# Revit family: CCIRC Emergency Circular Lighting_UK_Non-Hosted_R20_V1.0
name_source: partatom
category: Lighting Fixtures
units: mm (PartAtom-declared; Revit-internal decimal feet)

## family parameters
Always vertical = Yes
Cut with Voids When Loaded = No
Light Source = Yes
OmniClass Number = 23.80.70.00
OmniClass Title = Lighting
Part Type = Normal
Room Calculation Point = No
Round Connector Dimension = Use Diameter
Shared = No
Work Plane-Based = No

## types (2) — shared parameters
Applicable Standards = BS EN 60598.2.22, BS 5266
Battery Type = Lithium Iron Phosphate (LiFePO4)
Charging Method = Intelligent Current Limited Constant Voltage
Color Filter = 16777215
Construction = Polycarbonate
Diffuser = Polycarbonate Diffuser
Dimensions (L x W x H) = 327mm (Diameter) x 100mm (Height)
Dimming Lamp Color Temperature Shift = <None>
Emergency Lumen Output = 374lm
Emit Shape Visible in Rendering = No
IP Rating = IP54
LED Driver = LED Driver -11W Stallion, 360mA
Lamp = LED module, 4,000K natural white, 50,000h life, Ra>80
Manufacturer = Clevertronics
Mounting = Surface Mount
Operating Mode = Sustained
Operating Temperature = 0˚C to 30˚C
Operating Voltage = 220-240V AC; 50Hz
Photometric Web File = 6002_CCIRC-HV(S4)_EM220mA_23082021-02_IES2002.IES
Power Factor = 0.93
Replacement Battery = 1550230
Replacement Driver = 1330091
Replacement lamp = 8011800
Tilt Angle = 90.00°
Weight = 1.8 kg
zero-valued in all types: Default Elevation

## per-type parameters (varying)
| type | Description | MIC Number | Power Consumption (Lamp ON Max Charge) | Power Consumption (Lamp Off Standby) | Replacement Emergency Driver | Replacement Item | Testing System | Total Lumen Output |
| CCIRC | CLP Premium Circular LED Emergency Luminaire, Trim colourwhite | UKC02310010001 | 16.8 W | 1.0 W | UKM02370250001 |  | Clevertest Plus Enabled (Not activated by default) | 1460lm |
| CCIRC-HVG | CLP Premium Circular LED Emergency Luminaire, Trim colour white | UKC02810010002 | 17.3 W | 1.3 W | UKM02870200001 | 8003330 | Zoneworks XT HIVE (RF) | 1460lm @118lm/W |

note: column(s) folded — value = type name in every type: Model

## geometry (parser evidence)
native form markers: Sweep x3
no freeform markers — native parametric forms only
